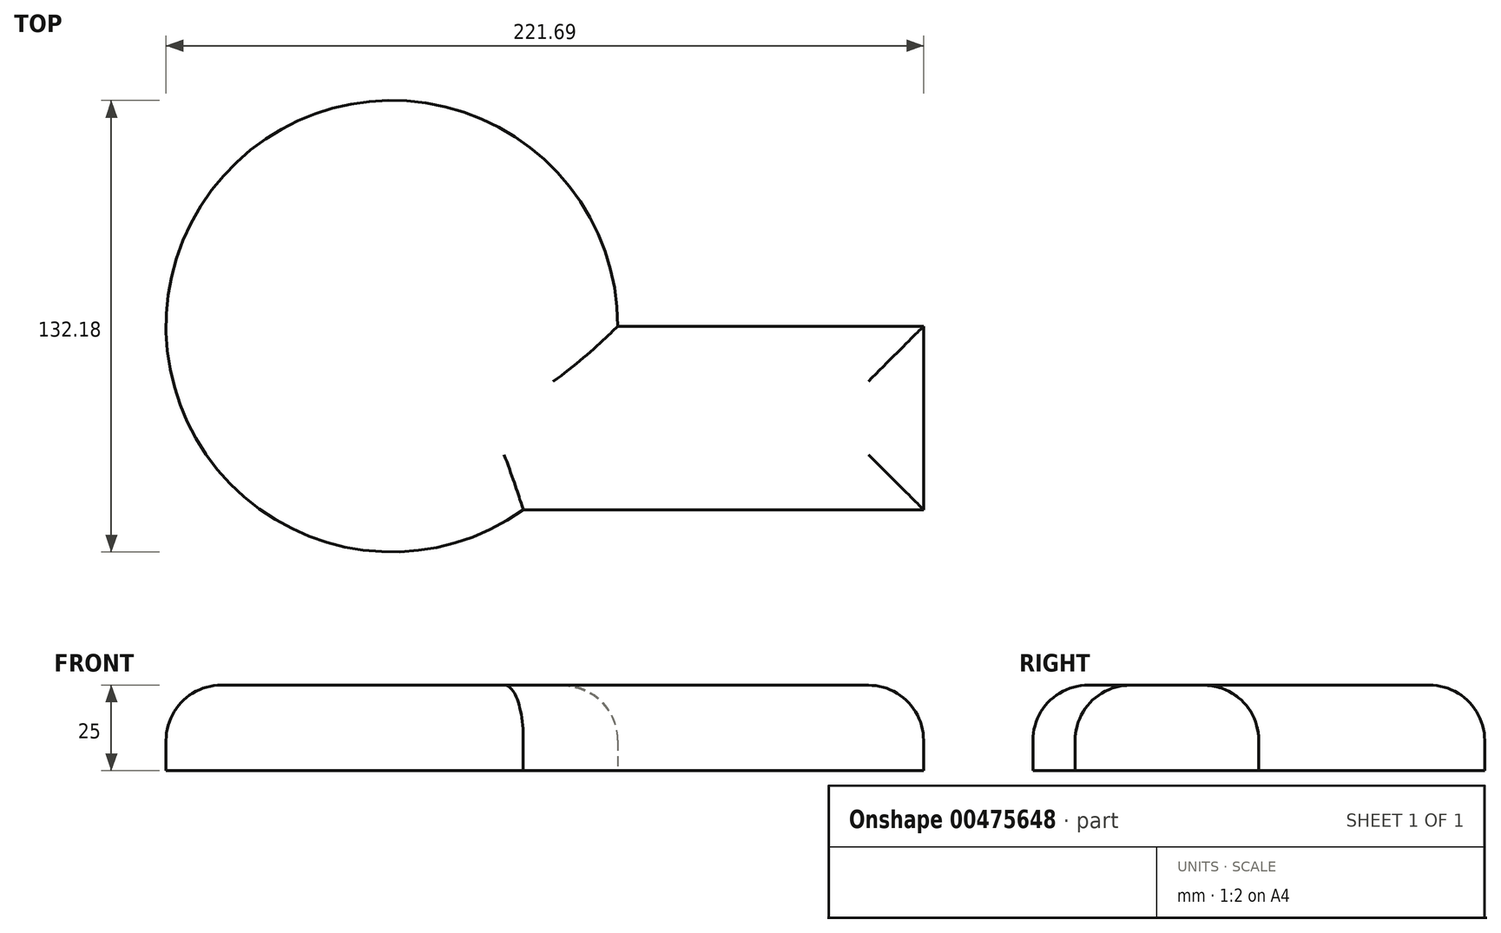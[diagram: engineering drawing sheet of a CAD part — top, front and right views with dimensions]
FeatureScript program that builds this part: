
annotation { "Feature Type Name" : "Feature", "Feature Type Description" : "" }
export const myFeature = defineFeature(function(context is Context, id is Id, definition is map)
    precondition{}
    {
        {
            var Q0;
            Q0=qCreatedBy(makeId("Top.planeOp"),FACE);
            var sketch = newSketch(context, id + "F0", { "sketchPlane" : qUnion([Q0])});
            skCircle(sketch, "E0", {"center": v(0, 0) * mm, "radius": 66.1 * mm});
            skLineSegment(sketch, "E1.bottom", {"start": v(0, 0) * mm, "end": v(155.6, 0) * mm});
            skLineSegment(sketch, "E1.top", {"start": v(0, -53.76) * mm, "end": v(155.6, -53.76) * mm});
            skLineSegment(sketch, "E1.left", {"start": v(0, 0) * mm, "end": v(0, -53.76) * mm});
            skLineSegment(sketch, "E1.right", {"start": v(155.6, 0) * mm, "end": v(155.6, -53.76) * mm});
            skSolve(sketch);
        }
        {
            var Q0;
            {var subQ5=sQuery(id+"F0.wireOp",EDGE,"E1.right");Q0=makeQuery(id+"F0.imprint","IMPRINT",FACE,{"disambiguationData":[TD([[makeQuery(id+"F0.imprint","IMPRINT",EDGE,{"derivedFrom":subQ5}),-1.0]])]});}
            var Q1;
            {var subQ5=sQuery(id+"F0.wireOp",EDGE,"E1.left");Q1=makeQuery(id+"F0.imprint","IMPRINT",FACE,{"disambiguationData":[TD([[makeQuery(id+"F0.imprint","IMPRINT",EDGE,{"derivedFrom":subQ5}),1.0]])]});}
            var Q2;
            {var subQ5=sQuery(id+"F0.wireOp",EDGE,"E1.left");Q2=makeQuery(id+"F0.imprint","IMPRINT",FACE,{"disambiguationData":[TD([[makeQuery(id+"F0.imprint","IMPRINT",EDGE,{"derivedFrom":subQ5}),-1.0]])]});}
            extrude(context, id + "F1", {"entities" : qUnion([Q0, Q1, Q2]), "depth" : 25 * mm});
        }
        {
            var Q0;
            Q0=makeQuery(id+"F1.opExtrude","CAP_EDGE",EDGE,{"disambiguationData":[OSD([sQuery(id+"F0.wireOp",EDGE,"E0")])],"isStart":false});
            var Q1;
            Q1=makeQuery(id+"F1.opExtrude","CAP_FACE",FACE,{"disambiguationData":[OSD([sQuery(id+"F0.wireOp",EDGE,"E0"),sQuery(id+"F0.wireOp",EDGE,"E1.bottom"),sQuery(id+"F0.wireOp",EDGE,"E1.top"),sQuery(id+"F0.wireOp",EDGE,"E1.right")])],"isStart":false});
            var Q2;
            Q2=makeQuery(id+"F1.opExtrude","CAP_EDGE",EDGE,{"disambiguationData":[OSD([sQuery(id+"F0.wireOp",EDGE,"E1.right")])],"isStart":false});
            fillet(context, id + "F2", {"entities" : qUnion([Q0, Q1, Q2]), "radius" : 16.18 * mm, "tangentPropagation" : true, "allowEdgeOverflow" : false});
        }
    });
